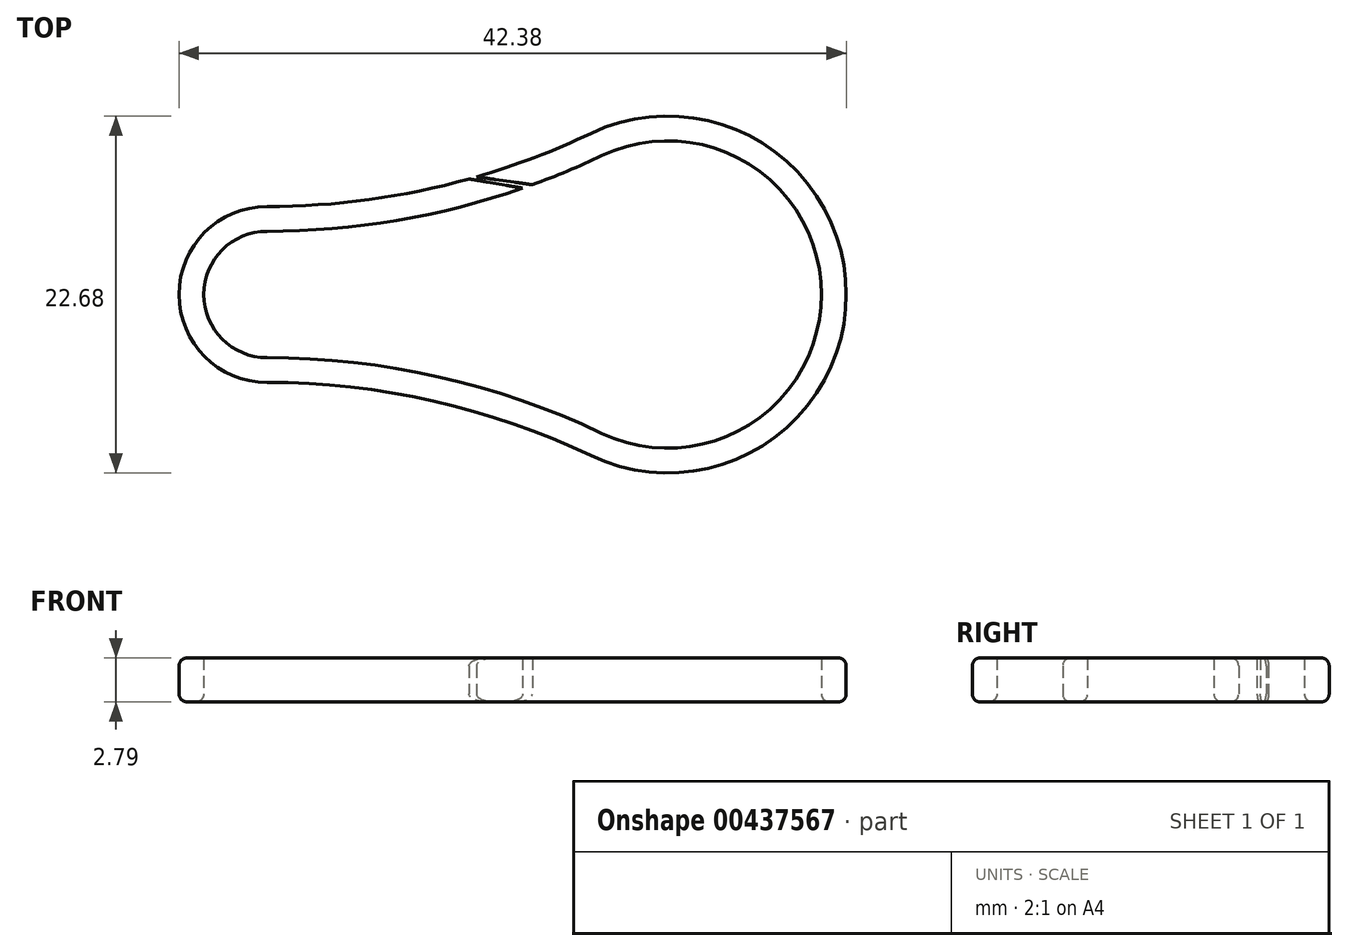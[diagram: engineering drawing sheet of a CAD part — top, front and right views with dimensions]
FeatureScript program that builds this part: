
annotation { "Feature Type Name" : "Feature", "Feature Type Description" : "" }
export const myFeature = defineFeature(function(context is Context, id is Id, definition is map)
    precondition{}
    {
        {
            var Q0;
            Q0=qCreatedBy(makeId("Top.planeOp"),FACE);
            var sketch = newSketch(context, id + "F0", { "sketchPlane" : qUnion([Q0])});
            skArc(sketch, "E0", {"start": v(0, 5.59) * mm, "mid": v(-5.59, 0) * mm, "end": v(0, -5.59) * mm});
            skArc(sketch, "E1", {"start": v(20.58, -10.24) * mm, "mid": v(36.79, 0) * mm, "end": v(20.58, 10.24) * mm});
            skArc(sketch, "E2", {"start": v(0, 5.59) * mm, "mid": v(10.55, 6.76) * mm, "end": v(20.58, 10.24) * mm});
            skArc(sketch, "E3", {"start": v(20.58, -10.24) * mm, "mid": v(10.55, -6.76) * mm, "end": v(0, -5.59) * mm});
            skArc(sketch, "E4.0", {"start": v(0, 4.01) * mm, "mid": v(10.9, 5.23) * mm, "end": v(21.26, 8.81) * mm});
            skArc(sketch, "E4.1", {"start": v(0, 4.01) * mm, "mid": v(-4.01, 0) * mm, "end": v(0, -4.01) * mm});
            skArc(sketch, "E4.2", {"start": v(21.26, -8.81) * mm, "mid": v(10.9, -5.23) * mm, "end": v(0, -4.01) * mm});
            skArc(sketch, "E4.3", {"start": v(21.26, -8.81) * mm, "mid": v(35.21, 0) * mm, "end": v(21.26, 8.81) * mm});
            skLineSegment(sketch, "E5", {"start": v(16.25, 6.76) * mm, "end": v(12.84, 7.34) * mm});
            skLineSegment(sketch, "E6", {"start": v(12.84, 7.34) * mm, "end": v(16.85, 6.97) * mm});
            skLineSegment(sketch, "E7", {"start": v(16.85, 6.97) * mm, "end": v(13.31, 7.47) * mm});
            skSolve(sketch);
        }
        {
            var Q0;
            Q0=makeQuery(id+"F0.imprint","IMPRINT",FACE,{"disambiguationData":[TD([[makeQuery(id+"F0.imprint","IMPRINT",EDGE,{"derivedFrom":sQuery(id+"F0.wireOp",EDGE,"E0")}),1.0]])]});
            extrude(context, id + "F1", {"entities" : qUnion([Q0]), "depth" : 2.8 * mm});
        }
        {
            var Q0;
            Q0=makeQuery(id+"F1.opExtrude","CAP_EDGE",EDGE,{"disambiguationData":[OSD([sQuery(id+"F0.wireOp",EDGE,"E2")])],"isStart":true});
            var Q1;
            Q1=makeQuery(id+"F1.opExtrude","CAP_EDGE",EDGE,{"disambiguationData":[OSD([sQuery(id+"F0.wireOp",EDGE,"E2")])],"isStart":false});
            var Q2;
            Q2=makeQuery(id+"F1.opExtrude","CAP_EDGE",EDGE,{"disambiguationData":[OSD([sQuery(id+"F0.wireOp",EDGE,"E4.3")])],"isStart":true});
            fillet(context, id + "F2", {"entities" : qUnion([Q0, Q1, Q2]), "radius" : 0.5 * mm, "tangentPropagation" : true, "allowEdgeOverflow" : false});
        }
    });
